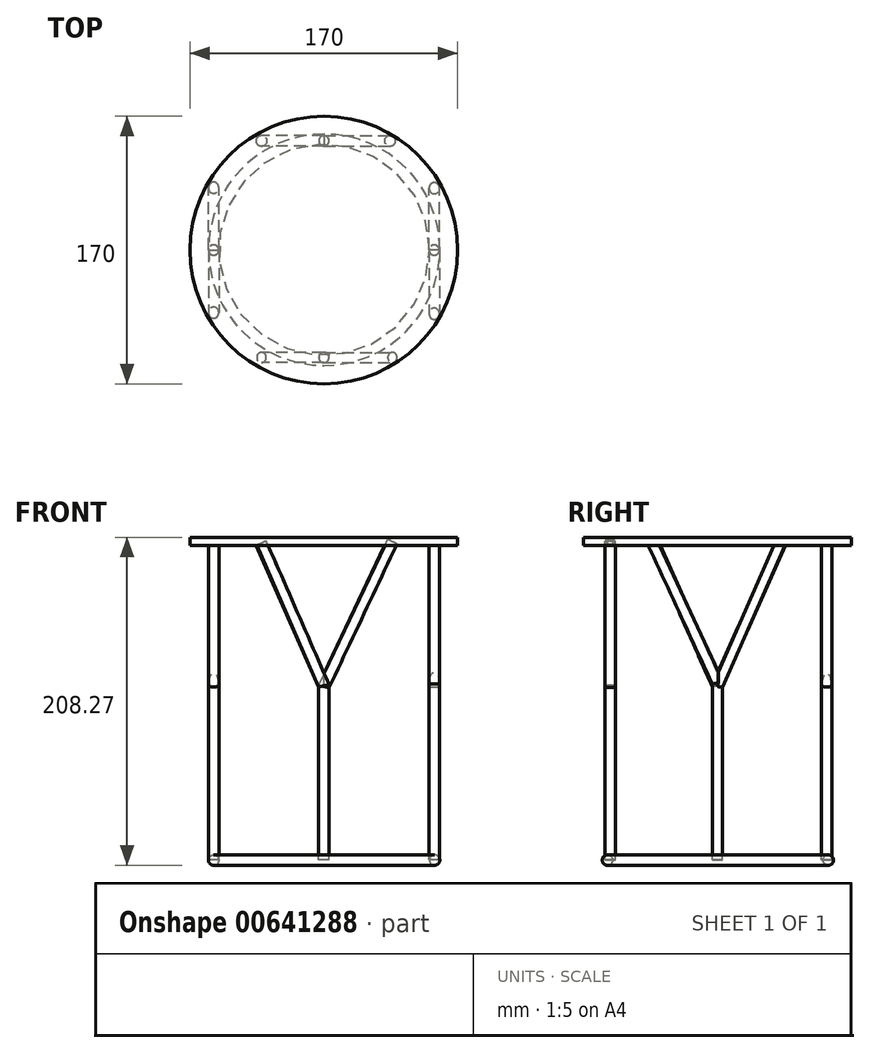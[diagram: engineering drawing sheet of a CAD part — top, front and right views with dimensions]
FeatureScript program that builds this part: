
annotation { "Feature Type Name" : "Feature", "Feature Type Description" : "" }
export const myFeature = defineFeature(function(context is Context, id is Id, definition is map)
    precondition{}
    {
        {
            var Q0;
            Q0=qCreatedBy(makeId("Top.planeOp"),FACE);
            cPlane(context, id + "F0", {"entities" : qUnion([Q0]), "cplaneType" : CPlaneType.OFFSET, "offset" : 200 * mm, "width" : 152.4 * mm, "height" : 152.4 * mm});
        }
        {
            var Q0;
            Q0=qCreatedBy(id+"F0.planeOp",FACE);
            var sketch = newSketch(context, id + "F1", { "sketchPlane" : qUnion([Q0])});
            skCircle(sketch, "E0", {"center": v(0, 0) * mm, "radius": 85 * mm});
            skSolve(sketch);
        }
        {
            var Q0;
            Q0=makeQuery(id+"F1.imprint","IMPRINT",FACE,{"disambiguationData":[TD([[makeQuery(id+"F1.imprint","IMPRINT",EDGE,{"derivedFrom":sQuery(id+"F1.wireOp",EDGE,"E0")}),1.0]])]});
            extrude(context, id + "F2", {"entities" : qUnion([Q0]), "depth" : 5 * mm, "offsetDistance" : 25 * mm});
        }
        {
            var Q0;
            Q0=qCreatedBy(makeId("Top.planeOp"),FACE);
            var sketch = newSketch(context, id + "F3", { "sketchPlane" : qUnion([Q0])});
            skCircle(sketch, "E1", {"center": v(0, -68.25) * mm, "radius": 3.27 * mm});
            skSolve(sketch);
        }
        {
            var Q0;
            Q0=qCreatedBy(makeId("Front.planeOp"),FACE);
            cPlane(context, id + "F4", {"entities" : qUnion([Q0]), "cplaneType" : CPlaneType.OFFSET, "offset" : 70 * mm, "width" : 150 * mm, "height" : 150 * mm});
        }
        {
            var Q0;
            Q0=qCreatedBy(id+"F4.planeOp",FACE);
            var sketch = newSketch(context, id + "F5", { "sketchPlane" : qUnion([Q0])});
            skLineSegment(sketch, "E2", {"start": v(0, 0) * mm, "end": v(0, 110.3) * mm});
            skLineSegment(sketch, "E3", {"start": v(0, 110.3) * mm, "end": v(-41, 202.26) * mm});
            skLineSegment(sketch, "E4", {"start": v(0, 110.3) * mm, "end": v(43.5, 202.26) * mm});
            skSolve(sketch);
        }
        {
            var Q0;
            Q0=qCreatedBy(makeId("Right.planeOp"),FACE);
            cPlane(context, id + "F6", {"entities" : qUnion([Q0]), "cplaneType" : CPlaneType.OFFSET, "offset" : 70 * mm, "width" : 150 * mm, "height" : 150 * mm});
        }
        {
            var Q0;
            Q0=qCreatedBy(makeId("Front.planeOp"),FACE);
            cPlane(context, id + "F7", {"entities" : qUnion([Q0]), "cplaneType" : CPlaneType.OFFSET, "offset" : 70 * mm, "oppositeDirection" : true, "width" : 150 * mm, "height" : 150 * mm});
        }
        {
            var Q0;
            Q0=qCreatedBy(makeId("Right.planeOp"),FACE);
            cPlane(context, id + "F8", {"entities" : qUnion([Q0]), "cplaneType" : CPlaneType.OFFSET, "offset" : 70 * mm, "oppositeDirection" : true, "width" : 150 * mm, "height" : 150 * mm});
        }
        {
            var Q0;
            Q0=qCreatedBy(id+"F6.planeOp",FACE);
            var sketch = newSketch(context, id + "F9", { "sketchPlane" : qUnion([Q0])});
            skLineSegment(sketch, "E5", {"start": v(0, 0) * mm, "end": v(0, 110.3) * mm});
            skLineSegment(sketch, "E6", {"start": v(0, 110.3) * mm, "end": v(40.1, 201.8) * mm});
            skSolve(sketch);
        }
        {
            var Q0;
            Q0=qCreatedBy(id+"F7.planeOp",FACE);
            var sketch = newSketch(context, id + "F10", { "sketchPlane" : qUnion([Q0])});
            skLineSegment(sketch, "E7", {"start": v(0, 0) * mm, "end": v(0, 110.75) * mm});
            skLineSegment(sketch, "E8", {"start": v(0, 110.75) * mm, "end": v(42.8, 201.8) * mm});
            skSolve(sketch);
        }
        {
            var Q0;
            Q0=qCreatedBy(id+"F8.planeOp",FACE);
            var sketch = newSketch(context, id + "F11", { "sketchPlane" : qUnion([Q0])});
            skLineSegment(sketch, "E9", {"start": v(0, 0) * mm, "end": v(0, 110.75) * mm});
            skLineSegment(sketch, "E10", {"start": v(0, 110.75) * mm, "end": v(40.8, 202.71) * mm});
            skSolve(sketch);
        }
        {
            var Q0;
            Q0=makeQuery(id+"F3.imprint","IMPRINT",FACE,{"disambiguationData":[TD([[makeQuery(id+"F3.imprint","IMPRINT",EDGE,{"derivedFrom":sQuery(id+"F3.wireOp",EDGE,"E1")}),1.0]])]});
            var Q1;
            Q1=sQuery(id+"F5.wireOp",EDGE,"E2");
            var Q2;
            Q2=sQuery(id+"F5.wireOp",EDGE,"E4");
            sweep(context, id + "F12", {"profiles" : qUnion([Q0]), "path" : qUnion([Q1, Q2])});
        }
        {
            var Q0;
            Q0=qCreatedBy(id+"F4.planeOp",FACE);
            var sketch = newSketch(context, id + "F13", { "sketchPlane" : qUnion([Q0])});
            skLineSegment(sketch, "E11", {"start": v(0, 0) * mm, "end": v(0, 110.75) * mm});
            skLineSegment(sketch, "E12", {"start": v(0, 110.75) * mm, "end": v(-39.64, 201.35) * mm});
            skSolve(sketch);
        }
        {
            var Q0;
            Q0 = qSketchRegion(id + "F3", true);
            var Q1;
            Q1 = qConstructionFilter(qBodyType(qCreatedBy(id + "F13" ,EDGE), BodyType.WIRE), ConstructionObject.NO);
            sweep(context, id + "F14", {"profiles" : qUnion([Q0]), "path" : qUnion([Q1])});
        }
        {
            var Q0;
            Q0=qCreatedBy(makeId("Top.planeOp"),FACE);
            var sketch = newSketch(context, id + "F15", { "sketchPlane" : qUnion([Q0])});
            skCircle(sketch, "E13", {"center": v(0, 69.38) * mm, "radius": 3.27 * mm});
            skSolve(sketch);
        }
        {
            var Q0;
            Q0=qCreatedBy(makeId("Top.planeOp"),FACE);
            var sketch = newSketch(context, id + "F16", { "sketchPlane" : qUnion([Q0])});
            skCircle(sketch, "E14", {"center": v(70.06, 0) * mm, "radius": 3.27 * mm});
            skSolve(sketch);
        }
        {
            var Q0;
            Q0=qCreatedBy(makeId("Top.planeOp"),FACE);
            var sketch = newSketch(context, id + "F17", { "sketchPlane" : qUnion([Q0])});
            skCircle(sketch, "E15", {"center": v(-70.02, 0) * mm, "radius": 3.27 * mm});
            skSolve(sketch);
        }
        {
            var Q0;
            Q0=makeQuery(id+"F17.imprint","IMPRINT",FACE,{"disambiguationData":[TD([[makeQuery(id+"F17.imprint","IMPRINT",EDGE,{"derivedFrom":sQuery(id+"F17.wireOp",EDGE,"E15")}),1.0]])]});
            var Q1;
            Q1=sQuery(id+"F11.wireOp",EDGE,"E9");
            var Q2;
            Q2=sQuery(id+"F11.wireOp",EDGE,"E10");
            sweep(context, id + "F18", {"operationType" : NewBodyOperationType.ADD, "profiles" : qUnion([Q0]), "path" : qUnion([Q1, Q2])});
        }
        {
            var Q0;
            Q0=qCreatedBy(id+"F8.planeOp",FACE);
            var sketch = newSketch(context, id + "F19", { "sketchPlane" : qUnion([Q0])});
            skLineSegment(sketch, "E16", {"start": v(0, 0) * mm, "end": v(0, 110.75) * mm});
            skLineSegment(sketch, "E17", {"start": v(0, 110.75) * mm, "end": v(-40.54, 201.8) * mm});
            skSolve(sketch);
        }
        {
            var Q0;
            Q0 = qSketchRegion(id + "F17", true);
            var Q1;
            Q1 = qConstructionFilter(qBodyType(qCreatedBy(id + "F19" ,EDGE), BodyType.WIRE), ConstructionObject.NO);
            sweep(context, id + "F20", {"operationType" : NewBodyOperationType.ADD, "profiles" : qUnion([Q0]), "path" : qUnion([Q1])});
        }
        {
            var Q0;
            Q0=makeQuery(id+"F16.imprint","IMPRINT",FACE,{"disambiguationData":[TD([[makeQuery(id+"F16.imprint","IMPRINT",EDGE,{"derivedFrom":sQuery(id+"F16.wireOp",EDGE,"E14")}),1.0]])]});
            var Q1;
            Q1=sQuery(id+"F9.wireOp",EDGE,"E5");
            var Q2;
            Q2=sQuery(id+"F9.wireOp",EDGE,"E6");
            sweep(context, id + "F21", {"operationType" : NewBodyOperationType.ADD, "profiles" : qUnion([Q0]), "path" : qUnion([Q1, Q2])});
        }
        {
            var Q0;
            Q0=qCreatedBy(id+"F6.planeOp",FACE);
            var sketch = newSketch(context, id + "F22", { "sketchPlane" : qUnion([Q0])});
            skLineSegment(sketch, "E18", {"start": v(0, 0) * mm, "end": v(0, 112.57) * mm});
            skLineSegment(sketch, "E19", {"start": v(0, 112.57) * mm, "end": v(-41.9, 203.17) * mm});
            skSolve(sketch);
        }
        {
            var Q0;
            Q0 = qSketchRegion(id + "F16", true);
            var Q1;
            Q1 = qConstructionFilter(qBodyType(qCreatedBy(id + "F22" ,EDGE), BodyType.WIRE), ConstructionObject.NO);
            sweep(context, id + "F23", {"operationType" : NewBodyOperationType.ADD, "profiles" : qUnion([Q0]), "path" : qUnion([Q1])});
        }
        {
            var Q0;
            Q0=qCreatedBy(id+"F7.planeOp",FACE);
            var sketch = newSketch(context, id + "F24", { "sketchPlane" : qUnion([Q0])});
            skLineSegment(sketch, "E20", {"start": v(0, 0) * mm, "end": v(0, 110.75) * mm});
            skLineSegment(sketch, "E21", {"start": v(0, 110.75) * mm, "end": v(-41, 203.17) * mm});
            skSolve(sketch);
        }
        {
            var Q0;
            Q0 = qSketchRegion(id + "F15", true);
            var Q1;
            Q1 = qConstructionFilter(qBodyType(qCreatedBy(id + "F10" ,EDGE), BodyType.WIRE), ConstructionObject.NO);
            sweep(context, id + "F25", {"operationType" : NewBodyOperationType.ADD, "profiles" : qUnion([Q0]), "path" : qUnion([Q1])});
        }
        {
            var Q0;
            Q0 = qSketchRegion(id + "F15", true);
            var Q1;
            Q1 = qConstructionFilter(qBodyType(qCreatedBy(id + "F24" ,EDGE), BodyType.WIRE), ConstructionObject.NO);
            sweep(context, id + "F26", {"operationType" : NewBodyOperationType.ADD, "profiles" : qUnion([Q0]), "path" : qUnion([Q1])});
        }
        {
            var Q0;
            Q0=qCreatedBy(makeId("Front.planeOp"),FACE);
            var sketch = newSketch(context, id + "F27", { "sketchPlane" : qUnion([Q0])});
            skCircle(sketch, "E22", {"center": v(-70.03, 0) * mm, "radius": 3.28 * mm});
            skSolve(sketch);
        }
        {
            var Q0;
            Q0=qCreatedBy(makeId("Top.planeOp"),FACE);
            var sketch = newSketch(context, id + "F28", { "sketchPlane" : qUnion([Q0])});
            skCircle(sketch, "E23", {"center": v(0.16, 0.2) * mm, "radius": 67.5 * mm});
            skPoint(sketch, "E23.first.point", {"position": v(-67.34, 0) * mm});
            skPoint(sketch, "E23.second.point", {"position": v(67.66, 0) * mm});
            skPoint(sketch, "E23.third.point", {"position": v(0, 67.7) * mm});
            skSolve(sketch);
        }
        {
            var Q0;
            Q0 = qSketchRegion(id + "F27", true);
            var Q1;
            Q1 = qConstructionFilter(qBodyType(qCreatedBy(id + "F28" ,EDGE), BodyType.WIRE), ConstructionObject.NO);
            sweep(context, id + "F29", {"profiles" : qUnion([Q0]), "path" : qUnion([Q1])});
        }
    });
